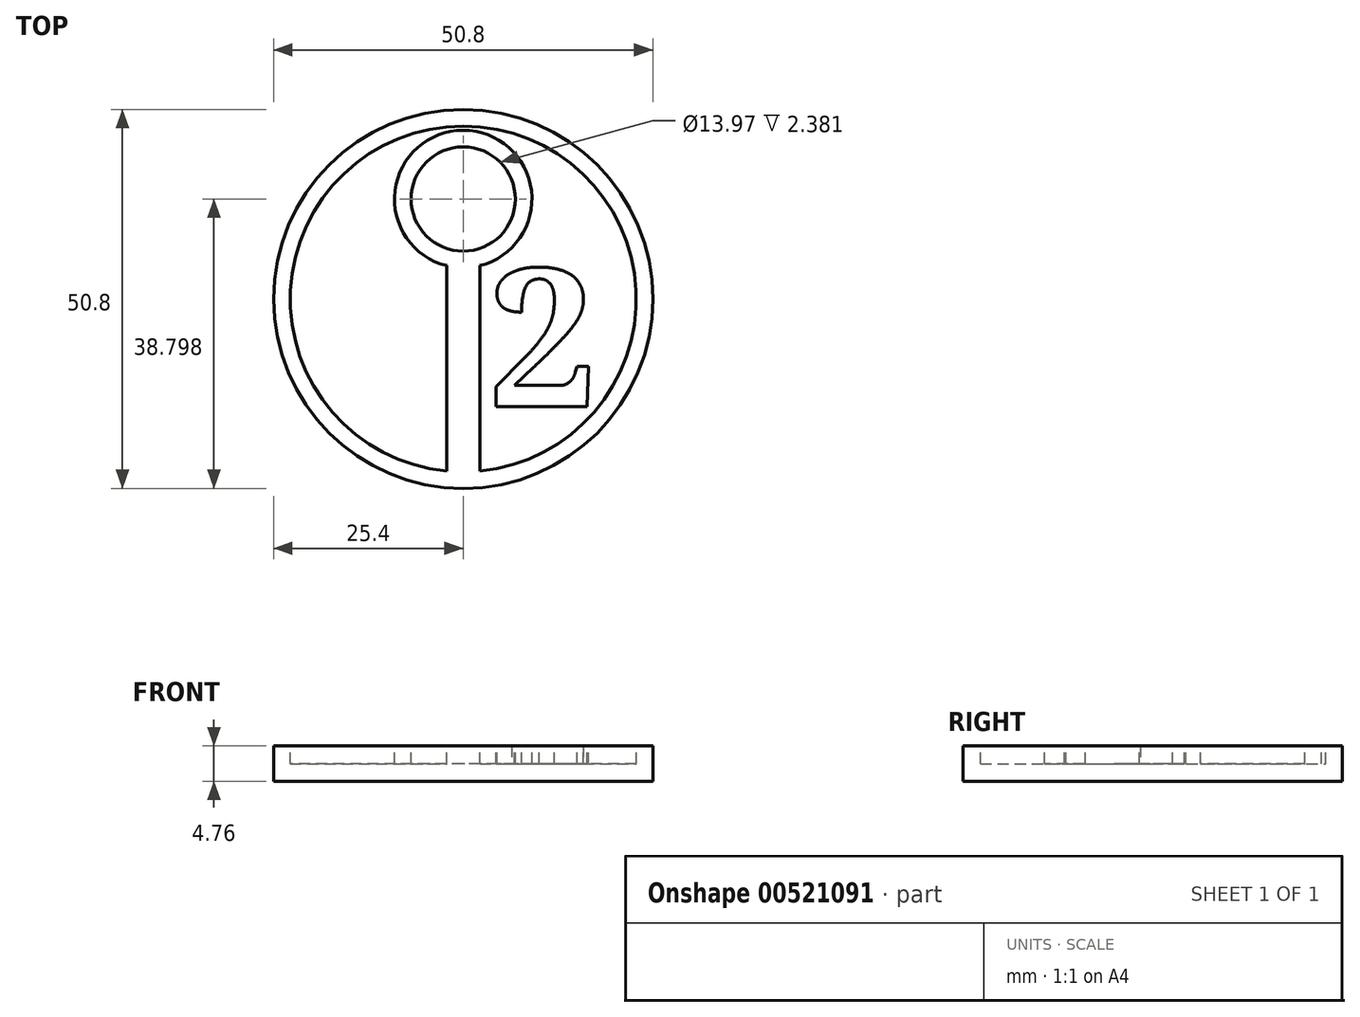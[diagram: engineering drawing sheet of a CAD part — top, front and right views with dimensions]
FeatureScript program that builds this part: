
annotation { "Feature Type Name" : "Feature", "Feature Type Description" : "" }
export const myFeature = defineFeature(function(context is Context, id is Id, definition is map)
    precondition{}
    {
        {
            var Q0;
            Q0=qCreatedBy(makeId("Top.planeOp"),FACE);
            var sketch = newSketch(context, id + "F0", { "sketchPlane" : qUnion([Q0])});
            skCircle(sketch, "E0", {"center": v(0, 0) * mm, "radius": 25.4 * mm});
            skSolve(sketch);
        }
        {
            var Q0;
            Q0=qSketchRegion(id+"F0",true);
            extrude(context, id + "F1", {"entities" : qUnion([Q0]), "depth" : 4.76 * mm, "offsetDistance" : 25.4 * mm});
        }
        {
            var Q0;
            Q0=makeQuery(id+"F1.opExtrude","CAP_FACE",FACE,{"disambiguationData":[OSD([sQuery(id+"F0.wireOp",EDGE,"E0")])],"isStart":false});
            var sketch = newSketch(context, id + "F2", { "sketchPlane" : qUnion([Q0])});
            skCircle(sketch, "E1", {"center": v(0, 0) * mm, "radius": 23.18 * mm});
            skCircle(sketch, "E2", {"center": v(0, 13.4) * mm, "radius": 6.99 * mm});
            skLineSegment(sketch, "E3.0", {"start": v(2.22, -23.07) * mm, "end": v(2.22, 4.46) * mm});
            skLineSegment(sketch, "E4", {"start": v(-2.22, 4.46) * mm, "end": v(-2.22, -23.07) * mm});
            skArc(sketch, "E5", {"start": v(2.22, 4.46) * mm, "mid": v(0, 22.6) * mm, "end": v(-2.22, 4.46) * mm});
            skSolve(sketch);
        }
        {
            var Q0;
            {var subQ0=sQuery(id+"F2.wireOp",EDGE,"E3.0");Q0=makeQuery(id+"F2.imprint","IMPRINT",FACE,{"disambiguationData":[TD([[makeQuery(id+"F2.imprint","IMPRINT",EDGE,{"derivedFrom":subQ0}),-1.0]])]});}
            extrude(context, id + "F3", {"entities" : qUnion([Q0]), "operationType" : NewBodyOperationType.REMOVE, "oppositeDirection" : true, "depth" : 2.38 * mm, "offsetDistance" : 25.4 * mm});
        }
        {
            var Q0;
            Q0=makeQuery(id+"F2.imprint","IMPRINT",FACE,{"disambiguationData":[TD([[makeQuery(id+"F2.imprint","IMPRINT",EDGE,{"derivedFrom":sQuery(id+"F2.wireOp",EDGE,"E2")}),1.0]])]});
            extrude(context, id + "F4", {"entities" : qUnion([Q0]), "operationType" : NewBodyOperationType.REMOVE, "oppositeDirection" : true, "depth" : 2.38 * mm, "offsetDistance" : 25.4 * mm});
        }
        {
            var Q0;
            {var subQ0=sQuery(id+"F2.wireOp",EDGE,"E3.0");Q0=makeQuery(id+"F2.imprint","IMPRINT",FACE,{"disambiguationData":[TD([[makeQuery(id+"F2.imprint","IMPRINT",EDGE,{"derivedFrom":subQ0}),-1.0]])]});}
            var sketch = newSketch(context, id + "F5", { "sketchPlane" : qUnion([Q0])});
            skLineSegment(sketch, "E6.bottom", {"start": v(3.5, 4.16) * mm, "end": v(18.42, 4.16) * mm});
            skLineSegment(sketch, "E6.right", {"start": v(18.42, 4.16) * mm, "end": v(18.42, -14.44) * mm});
            skText(sketch, "E7", { "text": "2", "fontName": "NotoSerif-Bold.ttf"});
            const initialGuessF5  = {"E7": [0.0035, -0.01444, 1, 0, 0.0186]};
            skSetInitialGuess(sketch, initialGuessF5);
            skSolve(sketch);
        }
        {
            var Q0;
            Q0=qSketchRegion(id+"F5",true);
            extrude(context, id + "F6", {"entities" : qUnion([Q0]), "operationType" : NewBodyOperationType.ADD, "oppositeDirection" : true, "depth" : 2.38 * mm, "offsetDistance" : 25.4 * mm});
        }
    });
